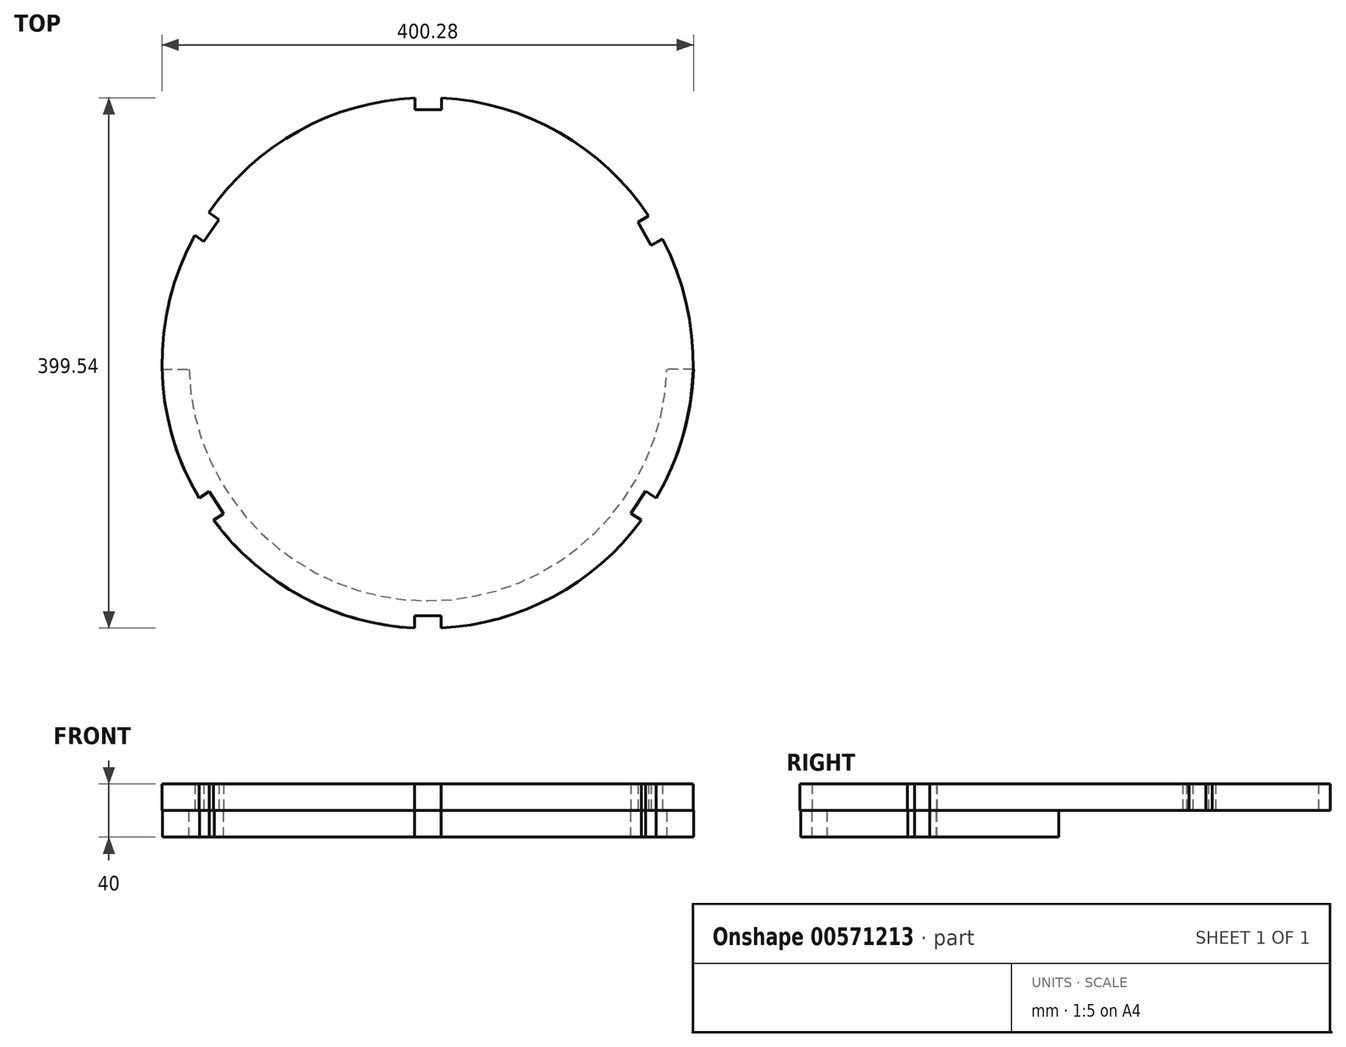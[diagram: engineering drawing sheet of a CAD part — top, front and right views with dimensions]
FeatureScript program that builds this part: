
annotation { "Feature Type Name" : "Feature", "Feature Type Description" : "" }
export const myFeature = defineFeature(function(context is Context, id is Id, definition is map)
    precondition{}
    {
        {
            var Q0;
            Q0=qCreatedBy(makeId("Top.planeOp"),FACE);
            var sketch = newSketch(context, id + "F0", { "sketchPlane" : qUnion([Q0])});
            skLineSegment(sketch, "E0", {"start": v(361.03, 12.44) * mm, "end": v(341.03, 12.44) * mm});
            skLineSegment(sketch, "E1", {"start": v(-38.97, 12.44) * mm, "end": v(-18.97, 12.44) * mm});
            skArc(sketch, "E2", {"start": v(-38.97, 12.44) * mm, "mid": v(161.03, -182.02) * mm, "end": v(361.03, 12.44) * mm});
            skArc(sketch, "E3", {"start": v(-18.97, 12.44) * mm, "mid": v(161.03, -161.96) * mm, "end": v(341.03, 12.44) * mm});
            skPoint(sketch, "E4.middle", {"position": v(161.03, -182.02) * mm});
            skSolve(sketch);
        }
        {
            var Q0;
            Q0 = qSketchRegion(id + "F0", true);
            extrude(context, id + "F1", {"entities" : qUnion([Q0]), "oppositeDirection" : true, "depth" : 20 * mm, "offsetDistance" : 25.4 * mm});
        }
        {
            var Q0;
            Q0=qCreatedBy(makeId("Top.planeOp"),FACE);
            var sketch = newSketch(context, id + "F2", { "sketchPlane" : qUnion([Q0])});
            skLineSegment(sketch, "E5.bottom", {"start": v(150.87, -173.28) * mm, "end": v(170.87, -173.28) * mm});
            skLineSegment(sketch, "E5.top", {"start": v(150.87, -183.28) * mm, "end": v(170.87, -183.28) * mm});
            skLineSegment(sketch, "E5.left", {"start": v(150.87, -173.28) * mm, "end": v(150.87, -183.28) * mm});
            skLineSegment(sketch, "E5.right", {"start": v(170.87, -173.28) * mm, "end": v(170.87, -183.28) * mm});
            skPoint(sketch, "E5.middle", {"position": v(160.87, -178.28) * mm});
            skSolve(sketch);
        }
        {
            var Q0;
            Q0 = qSketchRegion(id + "F2", true);
            extrude(context, id + "F3", {"entities" : qUnion([Q0]), "operationType" : NewBodyOperationType.REMOVE, "oppositeDirection" : true, "depth" : 20 * mm, "offsetDistance" : 25.4 * mm});
        }
        {
            var Q0;
            Q0=qCreatedBy(makeId("Top.planeOp"),FACE);
            var sketch = newSketch(context, id + "F4", { "sketchPlane" : qUnion([Q0])});
            skLineSegment(sketch, "E6", {"start": v(-1.27, -101.93) * mm, "end": v(7.1, -96.48) * mm});
            skLineSegment(sketch, "E7", {"start": v(7.1, -96.48) * mm, "end": v(-3.8, -79.7) * mm});
            skLineSegment(sketch, "E8", {"start": v(-3.8, -79.7) * mm, "end": v(-12.17, -85.16) * mm});
            skLineSegment(sketch, "E9", {"start": v(-12.17, -85.16) * mm, "end": v(-1.27, -101.93) * mm});
            skSolve(sketch);
        }
        {
            var Q0;
            Q0 = qSketchRegion(id + "F4", true);
            extrude(context, id + "F5", {"entities" : qUnion([Q0]), "operationType" : NewBodyOperationType.REMOVE, "oppositeDirection" : true, "depth" : 20 * mm, "offsetDistance" : 25.4 * mm});
        }
        {
            var Q0;
            Q0=qCreatedBy(makeId("Top.planeOp"),FACE);
            var sketch = newSketch(context, id + "F6", { "sketchPlane" : qUnion([Q0])});
            skLineSegment(sketch, "E10", {"start": v(322.21, -101.58) * mm, "end": v(313.85, -96.1) * mm});
            skLineSegment(sketch, "E11", {"start": v(313.85, -96.1) * mm, "end": v(324.82, -79.37) * mm});
            skLineSegment(sketch, "E12", {"start": v(324.82, -79.37) * mm, "end": v(333.18, -84.86) * mm});
            skLineSegment(sketch, "E13", {"start": v(322.21, -101.58) * mm, "end": v(333.18, -84.86) * mm});
            skSolve(sketch);
        }
        {
            var Q0;
            Q0 = qSketchRegion(id + "F6", true);
            extrude(context, id + "F7", {"entities" : qUnion([Q0]), "operationType" : NewBodyOperationType.REMOVE, "oppositeDirection" : true, "depth" : 20 * mm, "offsetDistance" : 25.4 * mm});
        }
        {
            var Q0;
            Q0=qCreatedBy(makeId("Top.planeOp"),FACE);
            var sketch = newSketch(context, id + "F8", { "sketchPlane" : qUnion([Q0])});
            skCircle(sketch, "E14", {"center": v(160.75, 17.19) * mm, "radius": 200 * mm});
            skSolve(sketch);
        }
        {
            var Q0;
            Q0 = qSketchRegion(id + "F8", true);
            extrude(context, id + "F9", {"entities" : qUnion([Q0]), "depth" : 20 * mm, "offsetDistance" : 25.4 * mm});
        }
        {
            var Q0;
            Q0 = qSketchRegion(id + "F6", true);
            var Q1;
            Q1 = qSketchRegion(id + "F4", true);
            extrude(context, id + "F10", {"entities" : qUnion([Q0, Q1]), "operationType" : NewBodyOperationType.REMOVE, "depth" : 20 * mm, "offsetDistance" : 25.4 * mm});
        }
        {
            var Q0;
            Q0 = qSketchRegion(id + "F2", true);
            extrude(context, id + "F11", {"entities" : qUnion([Q0]), "operationType" : NewBodyOperationType.REMOVE, "depth" : 20 * mm, "offsetDistance" : 25.4 * mm});
        }
        {
            var Q0;
            Q0 = qSketchRegion(id + "F6", true);
            var Q1;
            Q1 = qSketchRegion(id + "F4", true);
            var Q2;
            Q2 = qSketchRegion(id + "F2", true);
            extrude(context, id + "F12", {"entities" : qUnion([Q0, Q1, Q2]), "operationType" : NewBodyOperationType.REMOVE, "depth" : 20 * mm, "offsetDistance" : 25.4 * mm});
        }
        {
            var Q0;
            Q0=qCreatedBy(makeId("Top.planeOp"),FACE);
            var sketch = newSketch(context, id + "F13", { "sketchPlane" : qUnion([Q0])});
            skLineSegment(sketch, "E15", {"start": v(-15.91, 114.4) * mm, "end": v(-4.67, 130.95) * mm});
            skLineSegment(sketch, "E16", {"start": v(-15.91, 114.4) * mm, "end": v(-7.65, 108.78) * mm});
            skLineSegment(sketch, "E17", {"start": v(-7.65, 108.78) * mm, "end": v(3.6, 125.32) * mm});
            skLineSegment(sketch, "E18", {"start": v(-4.67, 130.95) * mm, "end": v(3.6, 125.32) * mm});
            skLineSegment(sketch, "E19.bottom", {"start": v(151.32, 207.97) * mm, "end": v(171.32, 207.97) * mm});
            skLineSegment(sketch, "E19.top", {"start": v(151.32, 217.97) * mm, "end": v(171.32, 217.97) * mm});
            skLineSegment(sketch, "E19.left", {"start": v(151.32, 207.97) * mm, "end": v(151.32, 217.97) * mm});
            skLineSegment(sketch, "E19.right", {"start": v(171.32, 207.97) * mm, "end": v(171.32, 217.97) * mm});
            skPoint(sketch, "E19.middle", {"position": v(161.32, 212.97) * mm});
            skLineSegment(sketch, "E20", {"start": v(337.66, 110.8) * mm, "end": v(327.89, 128.26) * mm});
            skLineSegment(sketch, "E21", {"start": v(327.89, 128.26) * mm, "end": v(319.16, 123.37) * mm});
            skLineSegment(sketch, "E22", {"start": v(319.16, 123.37) * mm, "end": v(328.93, 105.92) * mm});
            skLineSegment(sketch, "E23", {"start": v(328.93, 105.92) * mm, "end": v(337.66, 110.8) * mm});
            skSolve(sketch);
        }
        {
            var Q0;
            Q0 = qSketchRegion(id + "F13", true);
            extrude(context, id + "F14", {"entities" : qUnion([Q0]), "operationType" : NewBodyOperationType.REMOVE, "depth" : 20 * mm, "offsetDistance" : 25.4 * mm});
        }
    });
